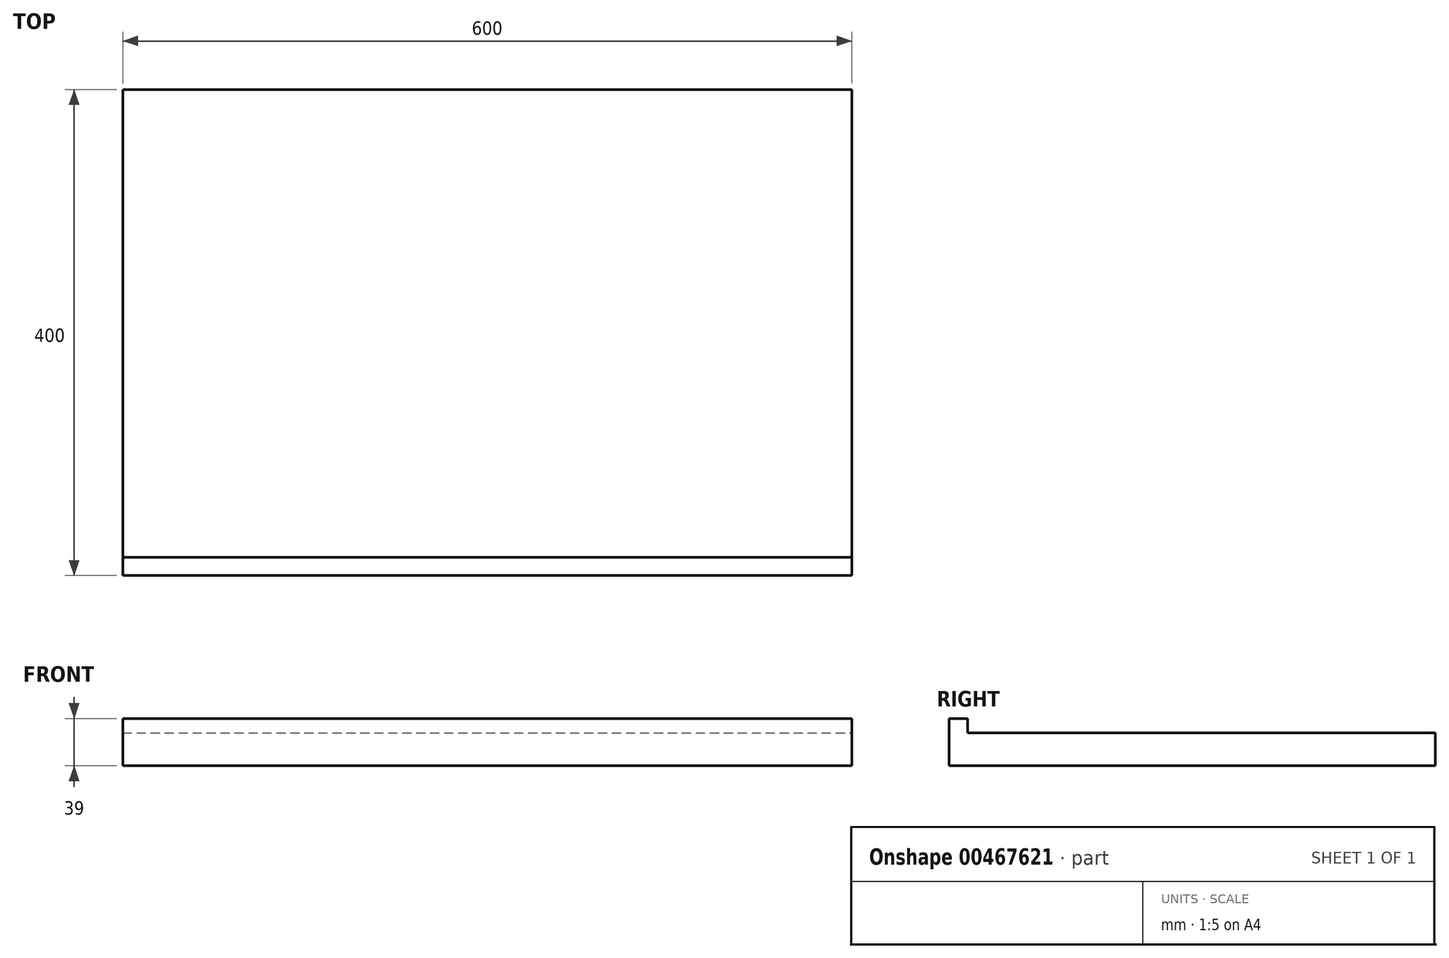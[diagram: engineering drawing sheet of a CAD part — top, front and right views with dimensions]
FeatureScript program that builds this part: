
annotation { "Feature Type Name" : "Feature", "Feature Type Description" : "" }
export const myFeature = defineFeature(function(context is Context, id is Id, definition is map)
    precondition{}
    {
        {
            var Q0;
            Q0=qCreatedBy(makeId("Top.planeOp"),FACE);
            var sketch = newSketch(context, id + "F0", { "sketchPlane" : qUnion([Q0])});
            skLineSegment(sketch, "E0.bottom", {"start": v(300, -200) * mm, "end": v(-300, -200) * mm});
            skLineSegment(sketch, "E0.left", {"start": v(300, -200) * mm, "end": v(300, 200) * mm});
            skLineSegment(sketch, "E0.right", {"start": v(-300, -200) * mm, "end": v(-300, 200) * mm});
            skPoint(sketch, "E0.middle", {"position": v(0, 0) * mm});
            skLineSegment(sketch, "E1", {"start": v(-300, 200) * mm, "end": v(300, 200) * mm});
            skSolve(sketch);
        }
        {
            var Q0;
            Q0=qSketchRegion(id+"F0",true);
            extrude(context, id + "F1", {"entities" : qUnion([Q0]), "depth" : 27 * mm});
        }
        {
            var Q0;
            Q0=makeQuery(id+"F1.opExtrude","CAP_FACE",FACE,{"disambiguationData":[OSD([sQuery(id+"F0.wireOp",EDGE,"E0.bottom"),sQuery(id+"F0.wireOp",EDGE,"E0.left"),sQuery(id+"F0.wireOp",EDGE,"E0.right"),sQuery(id+"F0.wireOp",EDGE,"E1")])],"isStart":false});
            var sketch = newSketch(context, id + "F2", { "sketchPlane" : qUnion([Q0])});
            skLineSegment(sketch, "E2.bottom", {"start": v(300, -200) * mm, "end": v(-300, -200) * mm});
            skLineSegment(sketch, "E2.top", {"start": v(300, -185) * mm, "end": v(-300, -185) * mm});
            skLineSegment(sketch, "E2.left", {"start": v(300, -200) * mm, "end": v(300, -185) * mm});
            skLineSegment(sketch, "E2.right", {"start": v(-300, -200) * mm, "end": v(-300, -185) * mm});
            skSolve(sketch);
        }
        {
            var Q0;
            Q0 = qSketchRegion(id + "F2", true);
            extrude(context, id + "F3", {"entities" : qUnion([Q0]), "operationType" : NewBodyOperationType.ADD, "depth" : 12 * mm});
        }
    });
